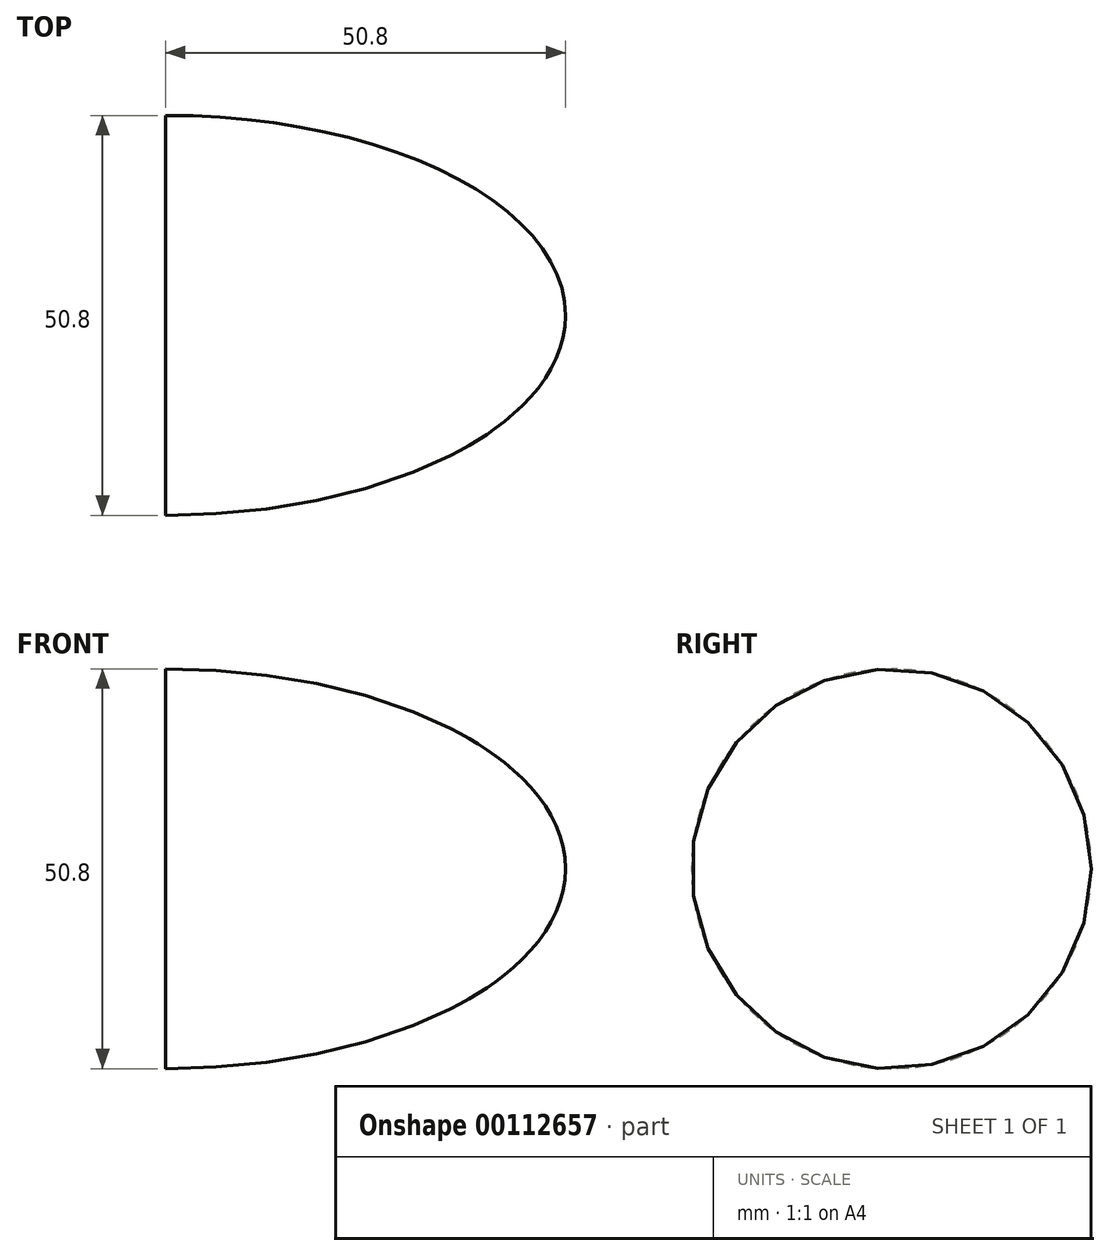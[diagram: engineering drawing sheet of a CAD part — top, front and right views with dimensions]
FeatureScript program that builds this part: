
annotation { "Feature Type Name" : "Feature", "Feature Type Description" : "" }
export const myFeature = defineFeature(function(context is Context, id is Id, definition is map)
    precondition{}
    {
        {
            var Q0;
            Q0=qCreatedBy(makeId("Top.planeOp"),FACE);
            var sketch = newSketch(context, id + "F0", { "sketchPlane" : qUnion([Q0])});
            skEllipse(sketch, "E0", {"center": v(0, 0) * mm, "majorRadius": 50.8 * mm, "minorRadius": 25.4 * mm, "majorAxis": v(-1, 0)});
            skLineSegment(sketch, "E1", {"start": v(50.8, 0) * mm, "end": v(-50.8, 0) * mm});
            skSolve(sketch);
        }
        {
            var Q0;
            Q0=qCreatedBy(makeId("Right.planeOp"),FACE);
            var sketch = newSketch(context, id + "F1", { "sketchPlane" : qUnion([Q0])});
            skCircle(sketch, "E2", {"center": v(0, 0) * mm, "radius": 50.8 * mm});
            skSolve(sketch);
        }
        {
            var Q0;
            {var subQ0=sQuery(id+"F0.wireOp",EDGE,"E1");Q0=makeQuery(id+"F0.imprint","IMPRINT",FACE,{"disambiguationData":[TD([[makeQuery(id+"F0.imprint","IMPRINT",EDGE,{"derivedFrom":subQ0}),-1.0]])]});}
            var Q1;
            Q1=sQuery(id+"F1.wireOp",EDGE,"E2");
            revolve(context, id + "F2", {"entities" : qUnion([Q0]), "axis" : qUnion([Q1]), "revolveType" : RevolveType.FULL});
        }
        {
            var Q0;
            Q0=qSketchRegion(id+"F1",true);
            var Q1;
            Q1=makeQuery(id+"F2.opRevolve","SWEPT_FACE",FACE,{"disambiguationData":[OSD([sQuery(id+"F0.wireOp",EDGE,"E0")])]});
            extrude(context, id + "F3", {"entities" : qUnion([Q0]), "operationType" : NewBodyOperationType.REMOVE, "endBound" : BoundingType.UP_TO_SURFACE, "oppositeDirection" : true, "endBoundEntityFace" : qUnion([Q1]), "depth" : 25.4 * mm});
        }
    });
